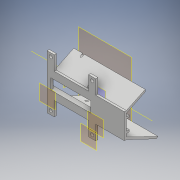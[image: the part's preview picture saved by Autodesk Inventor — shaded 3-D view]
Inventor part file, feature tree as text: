
AUTODESK INVENTOR PART (.ipt)
format: ipt  version: 2017 (Build 210142000, 142)  size: 258,048 bytes
history: native  units: mm
features: extrude x8, other x6, sketch x4, projected_geometry x1
ambient origin geometry x8: Origin, YZ Plane, XZ Plane, XY Plane, X Axis, Y Axis, Z Axis, Center Point
bodies: Solide1 (feature_tree)
feature tree (19):
  other  "Plan de construction16"
  extrude  "Extrusion11"  Depth=3.0mm
  other  "Plan de construction18"
  extrude  "Extrusion12"  Depth=3.0mm TaperAngle=0.0deg
  other  "Plan de construction19"
  sketch  "Esquisse14"
  other  "Plan de construction10"
  extrude  "Extrusion14"  Depth=10.0mm
  other  "Plan de construction11"
  extrude  "Extrusion15"  Depth=20.0mm
  extrude  "Extrusion16"  Depth=10.0mm
  other  "Plan de construction20"
  extrude  "Extrusion17"  Depth=20.0mm
  extrude  "Extrusion18"  Depth=4.5mm
  extrude  "Extrusion19"  Depth=4.5mm
  sketch  "Esquisse17"
  sketch  "Esquisse18"
  sketch  "Esquisse19"
  projected_geometry  "Boucle projetée9"
